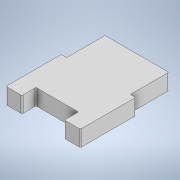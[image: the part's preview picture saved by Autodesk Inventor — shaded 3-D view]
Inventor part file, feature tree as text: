
AUTODESK INVENTOR PART (.ipt)
format: ipt  version: 2021 (Build 250183000, 183)  size: 126,976 bytes
history: native  units: mm
features: extrude x1, fillet x1, sketch x1
ambient origin geometry x8: Origin, YZ Plane, XZ Plane, XY Plane, X Axis, Y Axis, Z Axis, Center Point
bodies: Solid1 (feature_tree)
feature tree (3):
  extrude  "Extrusion1"  Depth=13.2mm
  fillet  "Fillet1"  Radius=40.0mm
  sketch  "Sketch1"  dims[d0=15.0mm d1=13.2mm d2=40.0mm d3=15.0mm d4=52.0mm d5=5.1mm d6=36.1mm d7=60.0mm d8=15.0mm d9=0.0mm d10=1.0mm]
